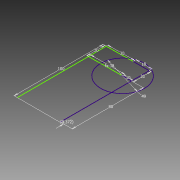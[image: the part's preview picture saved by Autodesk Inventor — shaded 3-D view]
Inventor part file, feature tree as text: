
AUTODESK INVENTOR PART (.ipt)
format: ipt  version: 2013 (Build 170138000, 138)  size: 72,704 bytes
history: native  units: mm
features: sketch x1
ambient origin geometry x8: Origin, YZ Plane, XZ Plane, XY Plane, X Axis, Y Axis, Z Axis, Center Point
feature tree (1):
  sketch  "Sketch1"  dims[d2=30.0mm d3=100.0mm d5=10.0mm d6=20.0mm d7=38.0mm d9=18.0mm d10=30.0mm d11=49.0mm d12=20.0mm d13=0.372mm d14=80.0mm]
